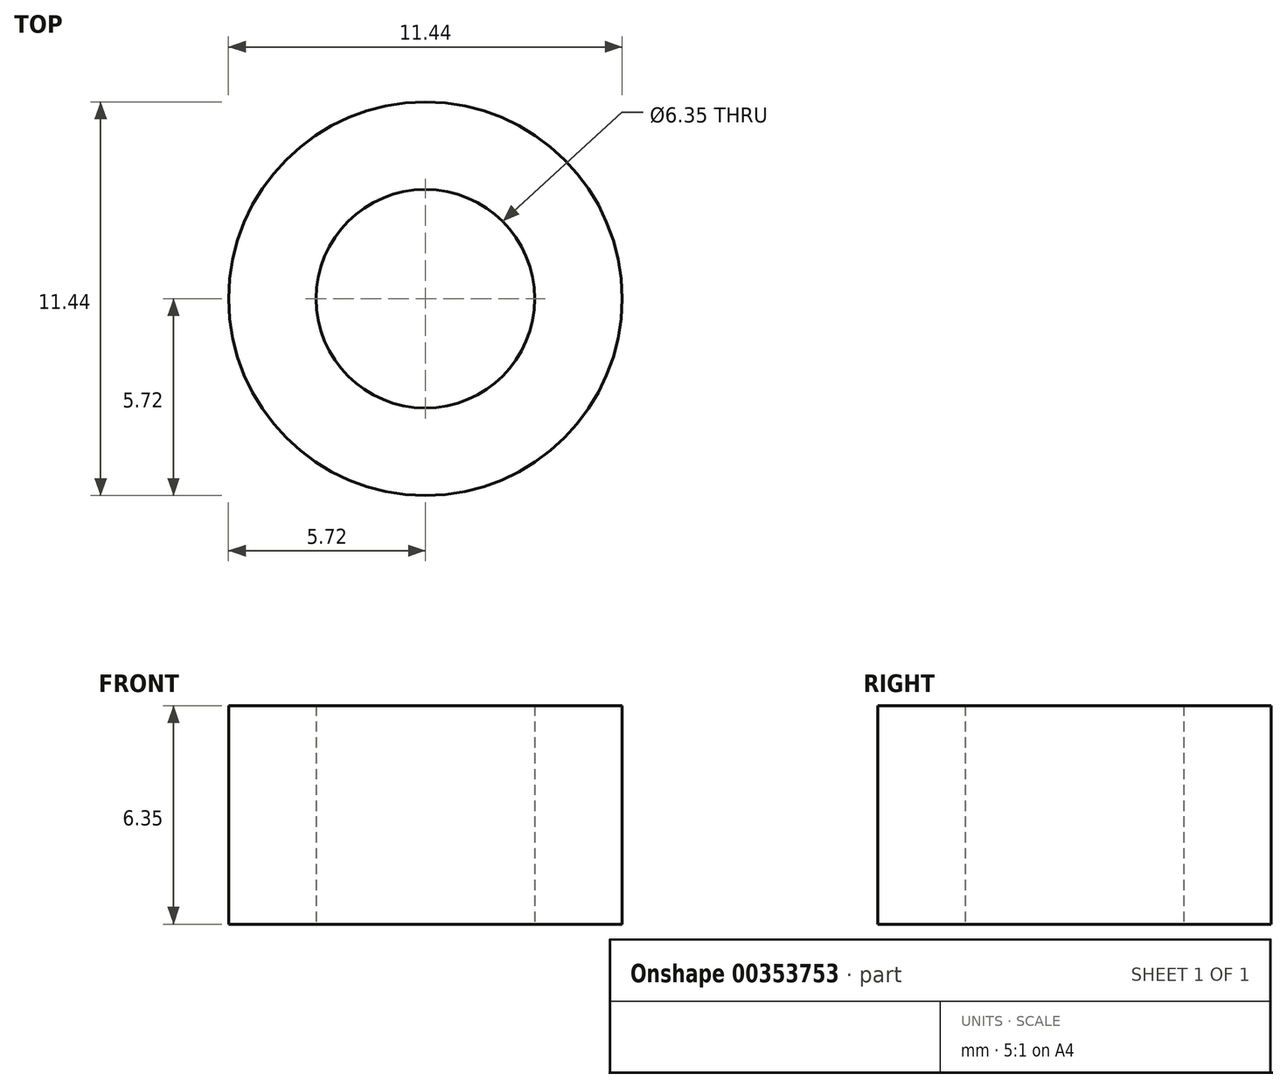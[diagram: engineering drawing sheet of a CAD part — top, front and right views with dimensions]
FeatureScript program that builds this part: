
annotation { "Feature Type Name" : "Feature", "Feature Type Description" : "" }
export const myFeature = defineFeature(function(context is Context, id is Id, definition is map)
    precondition{}
    {
        {
            var Q0;
            Q0=qCreatedBy(makeId("Top.planeOp"),FACE);
            var sketch = newSketch(context, id + "F0", { "sketchPlane" : qUnion([Q0])});
            skCircle(sketch, "E0", {"center": v(0, 0) * mm, "radius": 3.18 * mm});
            skCircle(sketch, "E1", {"center": v(0, 0) * mm, "radius": 5.72 * mm});
            skSolve(sketch);
        }
        {
            var Q0;
            Q0 = qSketchRegion(id + "F0", true);
            extrude(context, id + "F1", {"entities" : qUnion([Q0]), "depth" : 6.35 * mm});
        }
    });
